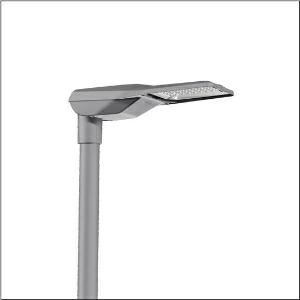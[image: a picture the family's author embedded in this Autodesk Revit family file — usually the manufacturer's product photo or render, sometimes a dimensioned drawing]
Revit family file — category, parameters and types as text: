
# Revit family: streetlight_sl_21_iq_mini___st1_0a_5xe2d41g08gb_82d1
name_source: partatom
category: Lighting Fixtures
units: mm (PartAtom-declared; Revit-internal decimal feet)

## family parameters
Cut with Voids When Loaded = No
Host = Face
Light Source = No
Part Type = Normal
Room Calculation Point = No
Round Connector Dimension = Use Diameter
Shared = No

## types (1)
- --- (1 x LED, 5920 lm, 37.1 W, 4000K)
    Apparent Load = 37 VA
    CIE Flux Codes = 37 72 97 100 100
    Color Rendering = 70
    Color Temperature = 4000K
    Default Elevation = 1800 mm
    Description = Streetlight SL 21 iQ mini, mast luminaire, primary light control with lens, of PMMA, primary optical cover: cover, of toughened safety glass, transparent, light distribution: ST1.0a, light emission: direct distribution, primary light characteristic: asymmetric, installation type: post-top, side-entry, LED, High Power LED, rated luminous flux: 5.920lm, luminous efficacy: 160lm/W, light colour: 740, colour temperature: 4000K, control: Street-Remote, Auto-Match, Temp-Guard, Lumen-Switch, Night-Set, Smart-Wire, Light-Fading, Desk-Remote (wireless, voltage-free reading and setting of iQ features in the workshop via application-optimized NFC function/RFID function), optimised constant luminous flux control (CLO 2.0), pre-setting: linear dimming characteristic, mains connection: 220..240V, AC, 50/60Hz, start of lifetime: 37W, end of service life: 39W, reduction: 18W, luminaire housing, of diecast aluminium, powder-coated, Siteco® metallic grey (DB 702S), corrosivity category C5 mid according to DIN EN ISO 12944, please order mast flange separately, inclination adjustable: 0°, 5°, 10°, 15°, sealing non-destructively replaceable, multi-level sealing system, length: 628mm, width: 235mm, height: 110mm, mast flange for spigot size: 42mm (side-entry): 5XC10008XM4, 60/48mm (side-entry/post-top): 5XC10108XM2, 76/60mm (side-entry/post-top): 5XC10108XM1, protection rating (complete): IP66, insulation class (complete): insulation class II (safety insulation), certification: CE, ENEC, ENEC+, VDE, impact resistance: IK09, permissible operating ambient temperature for outdoor applications: -40..+50°C, standard-compliant lighting for roads and squares, packaging unit: 1 piece

Light Distribution: ST1.0a
    Height = 110 mm
    Lamp = 1 x LED
    Lamp Light Flux = 5920 lm
    Lamp Power = 37.1 W
    Lamp count = 1
    Length = 625 mm
    Luminous efficacy = 160 lm/W
    Manufacturer = Siteco
    ModVariant = No
    Model = 5XE2D41G08GB
    Number of Poles = 1
    OnlyDefault = Yes
    Power Factor = 1
    Product Name = Streetlight SL 21 iQ mini | ST1.0a
    Product group = mast luminaire | pylon top
    ProductGroupID = 6100
    Protection Class = Protection class II
    Protection Degree = IP 66
    RLX_Detail_Level = 1
    RLX_Emergency_Light_Flux = 0 lm
    RLX_Emergency_Type = 0
    RLX_Emergency_Type_DB = No
    RlxData = <blob elided: 91985 chars, md5=cc07af2c>
    Socket = socket
    Standby Power = 0 W
    System Light Flux = 5920 lm
    System Power = 37 W
    Type Comments = factory setting: luminous flux: 100 % | dim-lin: 254 | 385 mA
    Type Image = l_1003519.jpg
    URL = http://relux.com
    VarID = @adj_160955
    Voltage = 0 V
    Weight = 0.00 kg
    Width = 234 mm

## geometry (parser evidence)
native form markers: Blend x4, Sweep x11
no freeform markers — native parametric forms only
